# Revit family: BLE-G-DBW-G6-E26
name_source: partatom
category: Lighting Fixtures
units: mm (PartAtom-declared; Revit-internal decimal feet)

## family parameters
Cut with Voids When Loaded = No
Host = Face
Light Source = Yes
Maintain Annotation Orientation = No
Part Type = Normal
Room Calculation Point = No
Round Connector Dimension = Use Diameter
Shared = No

## types (6) — shared parameters
Base Material = 100 - Black
Color Filter = 16777215
Default Elevation = 4' - 0"
Dimming Lamp Color Temperature Shift = <None>
Gooseneck Material = 100 - Black
Photometric Web File = generic
Shade Material = 100 - Black
Tilt Angle = 0.00°

## per-type parameters (varying)
| type | 10" | 12" | 14" | 16" | 20" | 24" |
| 12" | No | Yes | No | No | No | No |
| 14" | No | No | Yes | No | No | No |
| 16" | No | No | No | Yes | No | No |
| 10" | Yes | No | No | No | No | No |
| 20" | No | No | No | No | Yes | No |
| 24" | No | No | No | No | No | Yes |

## geometry (parser evidence)
native form markers: Sweep x31
no freeform markers — native parametric forms only
